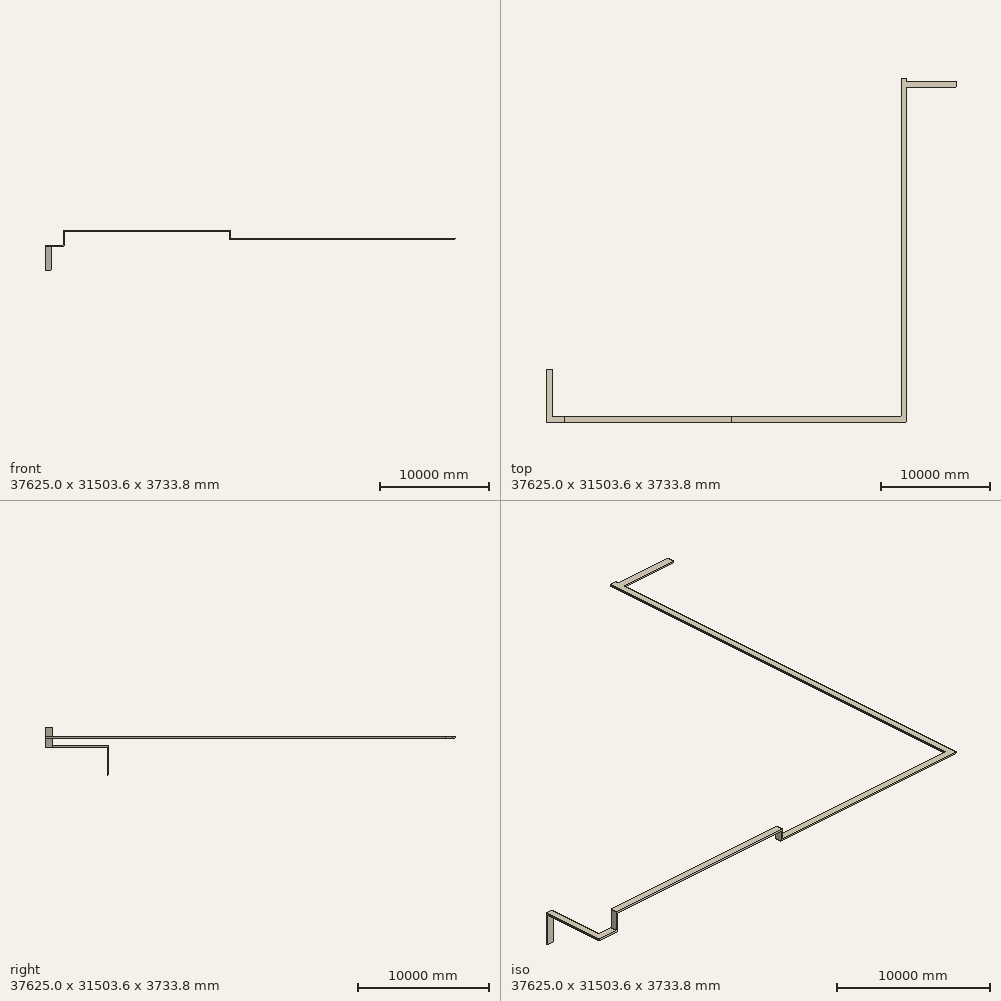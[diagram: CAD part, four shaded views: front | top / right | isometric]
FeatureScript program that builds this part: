
annotation { "Feature Type Name" : "Feature", "Feature Type Description" : "" }
export const myFeature = defineFeature(function(context is Context, id is Id, definition is map)
    precondition{}
    {
        {
            var Q0;
            Q0=qCreatedBy(makeId("Top.planeOp"),FACE);
            var sketch = newSketch(context, id + "F0", { "sketchPlane" : qUnion([Q0])});
            skLineSegment(sketch, "E0.bottom", {"start": v(0, 0) * mm, "end": v(-515.62, 0) * mm});
            skLineSegment(sketch, "E0.top", {"start": v(0, 127) * mm, "end": v(-515.62, 127) * mm});
            skLineSegment(sketch, "E0.left", {"start": v(0, 0) * mm, "end": v(0, 127) * mm});
            skLineSegment(sketch, "E0.right", {"start": v(-515.62, 0) * mm, "end": v(-515.62, 127) * mm});
            skSolve(sketch);
        }
        {
            var Q0;
            Q0=makeQuery(id+"F0.imprint","IMPRINT",FACE,{"disambiguationData":[TD([[makeQuery(id+"F0.imprint","IMPRINT",EDGE,{"derivedFrom":sQuery(id+"F0.wireOp",EDGE,"E0.bottom")}),-1.0]])]});
            extrude(context, id + "F1", {"entities" : qUnion([Q0]), "depth" : 2336.8 * mm});
        }
        {
            var Q0;
            Q0=makeQuery(id+"F1.opExtrude","SWEPT_FACE",FACE,{"disambiguationData":[OSD([sQuery(id+"F0.wireOp",EDGE,"E0.bottom")])]});
            var sketch = newSketch(context, id + "F2", { "sketchPlane" : qUnion([Q0])});
            skLineSegment(sketch, "E1.bottom", {"start": v(-515.62, 2336.8) * mm, "end": v(0, 2336.8) * mm});
            skLineSegment(sketch, "E1.top", {"start": v(-515.62, 2209.8) * mm, "end": v(0, 2209.8) * mm});
            skLineSegment(sketch, "E1.left", {"start": v(-515.62, 2336.8) * mm, "end": v(-515.62, 2209.8) * mm});
            skLineSegment(sketch, "E1.right", {"start": v(0, 2336.8) * mm, "end": v(0, 2209.8) * mm});
            skSolve(sketch);
        }
        {
            var Q0;
            Q0=makeQuery(id+"F2.imprint","IMPRINT",FACE,{"disambiguationData":[TD([[makeQuery(id+"F2.imprint","IMPRINT",EDGE,{"derivedFrom":sQuery(id+"F2.wireOp",EDGE,"E1.bottom")}),1.0]])]});
            extrude(context, id + "F3", {"entities" : qUnion([Q0]), "operationType" : NewBodyOperationType.ADD, "depth" : 4749.8 * mm});
        }
        {
            var Q0;
            Q0=makeQuery(id+"F3.boolean.opBoolean","MERGE",FACE,{"derivedFrom":[makeQuery(id+"F1.opExtrude","SWEPT_FACE",FACE,{"disambiguationData":[OSD([sQuery(id+"F0.wireOp",EDGE,"E0.left")])]}),makeQuery(id+"F3.opExtrude","SWEPT_FACE",FACE,{"disambiguationData":[OSD([sQuery(id+"F2.wireOp",EDGE,"E1.right")])]})]});
            var sketch = newSketch(context, id + "F4", { "sketchPlane" : qUnion([Q0])});
            skLineSegment(sketch, "E2.bottom", {"start": v(-4749.8, 2336.8) * mm, "end": v(-4234.18, 2336.8) * mm});
            skLineSegment(sketch, "E2.top", {"start": v(-4749.8, 2209.8) * mm, "end": v(-4234.18, 2209.8) * mm});
            skLineSegment(sketch, "E2.left", {"start": v(-4749.8, 2336.8) * mm, "end": v(-4749.8, 2209.8) * mm});
            skLineSegment(sketch, "E2.right", {"start": v(-4234.18, 2336.8) * mm, "end": v(-4234.18, 2209.8) * mm});
            skSolve(sketch);
        }
        {
            var Q0;
            Q0=makeQuery(id+"F4.imprint","IMPRINT",FACE,{"disambiguationData":[TD([[makeQuery(id+"F4.imprint","IMPRINT",EDGE,{"derivedFrom":sQuery(id+"F4.wireOp",EDGE,"E2.bottom")}),-1.0]])]});
            extrude(context, id + "F5", {"entities" : qUnion([Q0]), "operationType" : NewBodyOperationType.ADD, "depth" : 1219.2 * mm});
        }
        {
            var Q0;
            Q0=makeQuery(id+"F5.boolean.opBoolean","MERGE",FACE,{"derivedFrom":[makeQuery(id+"F3.boolean.opBoolean","MERGE",FACE,{"derivedFrom":[makeQuery(id+"F1.opExtrude","CAP_FACE",FACE,{"disambiguationData":[OSD([sQuery(id+"F0.wireOp",EDGE,"E0.bottom"),sQuery(id+"F0.wireOp",EDGE,"E0.top"),sQuery(id+"F0.wireOp",EDGE,"E0.left"),sQuery(id+"F0.wireOp",EDGE,"E0.right")])],"isStart":false}),makeQuery(id+"F3.opExtrude","SWEPT_FACE",FACE,{"disambiguationData":[OSD([sQuery(id+"F2.wireOp",EDGE,"E1.bottom")])]})]}),makeQuery(id+"F5.opExtrude","SWEPT_FACE",FACE,{"disambiguationData":[OSD([sQuery(id+"F4.wireOp",EDGE,"E2.bottom")])]})]});
            var sketch = newSketch(context, id + "F6", { "sketchPlane" : qUnion([Q0])});
            skLineSegment(sketch, "E3.bottom", {"start": v(1219.2, -4234.18) * mm, "end": v(1092.2, -4234.18) * mm});
            skLineSegment(sketch, "E3.top", {"start": v(1219.2, -4749.8) * mm, "end": v(1092.2, -4749.8) * mm});
            skLineSegment(sketch, "E3.left", {"start": v(1219.2, -4234.18) * mm, "end": v(1219.2, -4749.8) * mm});
            skLineSegment(sketch, "E3.right", {"start": v(1092.2, -4234.18) * mm, "end": v(1092.2, -4749.8) * mm});
            skSolve(sketch);
        }
        {
            var Q0;
            Q0=makeQuery(id+"F6.imprint","IMPRINT",FACE,{"disambiguationData":[TD([[makeQuery(id+"F6.imprint","IMPRINT",EDGE,{"derivedFrom":sQuery(id+"F6.wireOp",EDGE,"E3.bottom")}),1.0]])]});
            extrude(context, id + "F7", {"entities" : qUnion([Q0]), "operationType" : NewBodyOperationType.ADD, "depth" : 1397 * mm});
        }
        {
            var Q0;
            Q0=makeQuery(id+"F7.boolean.opBoolean","MERGE",FACE,{"derivedFrom":[makeQuery(id+"F5.opExtrude","CAP_FACE",FACE,{"disambiguationData":[OSD([sQuery(id+"F4.wireOp",EDGE,"E2.bottom"),sQuery(id+"F4.wireOp",EDGE,"E2.top"),sQuery(id+"F4.wireOp",EDGE,"E2.left"),sQuery(id+"F4.wireOp",EDGE,"E2.right")])],"isStart":false}),makeQuery(id+"F7.opExtrude","SWEPT_FACE",FACE,{"disambiguationData":[OSD([sQuery(id+"F6.wireOp",EDGE,"E3.left")])]})]});
            var sketch = newSketch(context, id + "F8", { "sketchPlane" : qUnion([Q0])});
            skLineSegment(sketch, "E4.bottom", {"start": v(-4749.8, 3733.8) * mm, "end": v(-4234.18, 3733.8) * mm});
            skLineSegment(sketch, "E4.top", {"start": v(-4749.8, 3606.8) * mm, "end": v(-4234.18, 3606.8) * mm});
            skLineSegment(sketch, "E4.left", {"start": v(-4749.8, 3733.8) * mm, "end": v(-4749.8, 3606.8) * mm});
            skLineSegment(sketch, "E4.right", {"start": v(-4234.18, 3733.8) * mm, "end": v(-4234.18, 3606.8) * mm});
            skSolve(sketch);
        }
        {
            var Q0;
            Q0=makeQuery(id+"F8.imprint","IMPRINT",FACE,{"disambiguationData":[TD([[makeQuery(id+"F8.imprint","IMPRINT",EDGE,{"derivedFrom":sQuery(id+"F8.wireOp",EDGE,"E4.bottom")}),-1.0]])]});
            extrude(context, id + "F9", {"entities" : qUnion([Q0]), "operationType" : NewBodyOperationType.ADD, "depth" : 15240 * mm});
        }
        {
            var Q0;
            Q0=makeQuery(id+"F9.opExtrude","SWEPT_FACE",FACE,{"disambiguationData":[OSD([sQuery(id+"F8.wireOp",EDGE,"E4.top")])]});
            var sketch = newSketch(context, id + "F10", { "sketchPlane" : qUnion([Q0])});
            skLineSegment(sketch, "E5.bottom", {"start": v(16459.2, 4749.8) * mm, "end": v(16332.2, 4749.8) * mm});
            skLineSegment(sketch, "E5.top", {"start": v(16459.2, 4234.18) * mm, "end": v(16332.2, 4234.18) * mm});
            skLineSegment(sketch, "E5.left", {"start": v(16459.2, 4749.8) * mm, "end": v(16459.2, 4234.18) * mm});
            skLineSegment(sketch, "E5.right", {"start": v(16332.2, 4749.8) * mm, "end": v(16332.2, 4234.18) * mm});
            skSolve(sketch);
        }
        {
            var Q0;
            Q0=makeQuery(id+"F10.imprint","IMPRINT",FACE,{"disambiguationData":[TD([[makeQuery(id+"F10.imprint","IMPRINT",EDGE,{"derivedFrom":sQuery(id+"F10.wireOp",EDGE,"E5.bottom")}),1.0]])]});
            extrude(context, id + "F11", {"entities" : qUnion([Q0]), "operationType" : NewBodyOperationType.ADD, "depth" : 736.6 * mm});
        }
        {
            var Q0;
            Q0=makeQuery(id+"F11.boolean.opBoolean","MERGE",FACE,{"derivedFrom":[makeQuery(id+"F9.opExtrude","CAP_FACE",FACE,{"disambiguationData":[OSD([sQuery(id+"F8.wireOp",EDGE,"E4.bottom"),sQuery(id+"F8.wireOp",EDGE,"E4.top"),sQuery(id+"F8.wireOp",EDGE,"E4.left"),sQuery(id+"F8.wireOp",EDGE,"E4.right")])],"isStart":false}),makeQuery(id+"F11.opExtrude","SWEPT_FACE",FACE,{"disambiguationData":[OSD([sQuery(id+"F10.wireOp",EDGE,"E5.left")])]})]});
            var sketch = newSketch(context, id + "F12", { "sketchPlane" : qUnion([Q0])});
            skLineSegment(sketch, "E6.bottom", {"start": v(-4234.18, 2870.2) * mm, "end": v(-4749.8, 2870.2) * mm});
            skLineSegment(sketch, "E6.top", {"start": v(-4234.18, 2997.2) * mm, "end": v(-4749.8, 2997.2) * mm});
            skLineSegment(sketch, "E6.left", {"start": v(-4234.18, 2870.2) * mm, "end": v(-4234.18, 2997.2) * mm});
            skLineSegment(sketch, "E6.right", {"start": v(-4749.8, 2870.2) * mm, "end": v(-4749.8, 2997.2) * mm});
            skSolve(sketch);
        }
        {
            var Q0;
            Q0=makeQuery(id+"F12.imprint","IMPRINT",FACE,{"disambiguationData":[TD([[makeQuery(id+"F12.imprint","IMPRINT",EDGE,{"derivedFrom":sQuery(id+"F12.wireOp",EDGE,"E6.bottom")}),1.0]])]});
            extrude(context, id + "F13", {"entities" : qUnion([Q0]), "operationType" : NewBodyOperationType.ADD, "depth" : 16078.2 * mm});
        }
        {
            var Q0;
            Q0=makeQuery(id+"F13.boolean.opBoolean","MERGE",FACE,{"derivedFrom":[makeQuery(id+"F11.boolean.opBoolean","MERGE",FACE,{"derivedFrom":[makeQuery(id+"F9.boolean.opBoolean","MERGE",FACE,{"derivedFrom":[makeQuery(id+"F7.boolean.opBoolean","MERGE",FACE,{"derivedFrom":[makeQuery(id+"F5.opExtrude","SWEPT_FACE",FACE,{"disambiguationData":[OSD([sQuery(id+"F4.wireOp",EDGE,"E2.right")])]}),makeQuery(id+"F7.opExtrude","SWEPT_FACE",FACE,{"disambiguationData":[OSD([sQuery(id+"F6.wireOp",EDGE,"E3.bottom")])]})]}),makeQuery(id+"F9.opExtrude","SWEPT_FACE",FACE,{"disambiguationData":[OSD([sQuery(id+"F8.wireOp",EDGE,"E4.right")])]})]}),makeQuery(id+"F11.opExtrude","SWEPT_FACE",FACE,{"disambiguationData":[OSD([sQuery(id+"F10.wireOp",EDGE,"E5.top")])]})]}),makeQuery(id+"F13.opExtrude","SWEPT_FACE",FACE,{"disambiguationData":[OSD([sQuery(id+"F12.wireOp",EDGE,"E6.left")])]})]});
            var sketch = newSketch(context, id + "F14", { "sketchPlane" : qUnion([Q0])});
            skLineSegment(sketch, "E7.bottom", {"start": v(-32537.4, 2997.2) * mm, "end": v(-32021.78, 2997.2) * mm});
            skLineSegment(sketch, "E7.top", {"start": v(-32537.4, 2870.2) * mm, "end": v(-32021.78, 2870.2) * mm});
            skLineSegment(sketch, "E7.left", {"start": v(-32537.4, 2997.2) * mm, "end": v(-32537.4, 2870.2) * mm});
            skLineSegment(sketch, "E7.right", {"start": v(-32021.78, 2997.2) * mm, "end": v(-32021.78, 2870.2) * mm});
            skSolve(sketch);
        }
        {
            var Q0;
            Q0=makeQuery(id+"F14.imprint","IMPRINT",FACE,{"disambiguationData":[TD([[makeQuery(id+"F14.imprint","IMPRINT",EDGE,{"derivedFrom":sQuery(id+"F14.wireOp",EDGE,"E7.bottom")}),-1.0]])]});
            extrude(context, id + "F15", {"entities" : qUnion([Q0]), "operationType" : NewBodyOperationType.ADD, "depth" : 30734 * mm});
        }
        {
            var Q0;
            Q0=makeQuery(id+"F15.boolean.opBoolean","MERGE",FACE,{"derivedFrom":[makeQuery(id+"F13.opExtrude","CAP_FACE",FACE,{"disambiguationData":[OSD([sQuery(id+"F12.wireOp",EDGE,"E6.bottom"),sQuery(id+"F12.wireOp",EDGE,"E6.top"),sQuery(id+"F12.wireOp",EDGE,"E6.left"),sQuery(id+"F12.wireOp",EDGE,"E6.right")])],"isStart":false}),makeQuery(id+"F15.opExtrude","SWEPT_FACE",FACE,{"disambiguationData":[OSD([sQuery(id+"F14.wireOp",EDGE,"E7.left")])]})]});
            var sketch = newSketch(context, id + "F16", { "sketchPlane" : qUnion([Q0])});
            skLineSegment(sketch, "E8.bottom", {"start": v(26499.82, 2870.2) * mm, "end": v(25984.2, 2870.2) * mm});
            skLineSegment(sketch, "E8.top", {"start": v(26499.82, 2997.2) * mm, "end": v(25984.2, 2997.2) * mm});
            skLineSegment(sketch, "E8.left", {"start": v(26499.82, 2870.2) * mm, "end": v(26499.82, 2997.2) * mm});
            skLineSegment(sketch, "E8.right", {"start": v(25984.2, 2870.2) * mm, "end": v(25984.2, 2997.2) * mm});
            skSolve(sketch);
        }
        {
            var Q0;
            Q0=makeQuery(id+"F16.imprint","IMPRINT",FACE,{"disambiguationData":[TD([[makeQuery(id+"F16.imprint","IMPRINT",EDGE,{"derivedFrom":sQuery(id+"F16.wireOp",EDGE,"E8.bottom")}),1.0]])]});
            extrude(context, id + "F17", {"entities" : qUnion([Q0]), "operationType" : NewBodyOperationType.ADD, "depth" : 3048 * mm});
        }
        {
            var Q0;
            Q0=makeQuery(id+"F17.boolean.opBoolean","MERGE",FACE,{"derivedFrom":[makeQuery(id+"F15.opExtrude","CAP_FACE",FACE,{"disambiguationData":[OSD([sQuery(id+"F14.wireOp",EDGE,"E7.bottom"),sQuery(id+"F14.wireOp",EDGE,"E7.top"),sQuery(id+"F14.wireOp",EDGE,"E7.left"),sQuery(id+"F14.wireOp",EDGE,"E7.right")])],"isStart":false}),makeQuery(id+"F17.opExtrude","SWEPT_FACE",FACE,{"disambiguationData":[OSD([sQuery(id+"F16.wireOp",EDGE,"E8.left")])]})]});
            var sketch = newSketch(context, id + "F18", { "sketchPlane" : qUnion([Q0])});
            skLineSegment(sketch, "E9.bottom", {"start": v(-32021.78, 2870.2) * mm, "end": v(-32537.4, 2870.2) * mm});
            skLineSegment(sketch, "E9.top", {"start": v(-32021.78, 2997.2) * mm, "end": v(-32537.4, 2997.2) * mm});
            skLineSegment(sketch, "E9.left", {"start": v(-32021.78, 2870.2) * mm, "end": v(-32021.78, 2997.2) * mm});
            skLineSegment(sketch, "E9.right", {"start": v(-32537.4, 2870.2) * mm, "end": v(-32537.4, 2997.2) * mm});
            skSolve(sketch);
        }
        {
            var Q0;
            Q0=makeQuery(id+"F18.imprint","IMPRINT",FACE,{"disambiguationData":[TD([[makeQuery(id+"F18.imprint","IMPRINT",EDGE,{"derivedFrom":sQuery(id+"F18.wireOp",EDGE,"E9.bottom")}),1.0]])]});
            extrude(context, id + "F19", {"entities" : qUnion([Q0]), "operationType" : NewBodyOperationType.ADD, "depth" : 254 * mm});
        }
        {
            var Q0;
            Q0=makeQuery(id+"F17.opExtrude","CAP_FACE",FACE,{"disambiguationData":[OSD([sQuery(id+"F16.wireOp",EDGE,"E8.bottom"),sQuery(id+"F16.wireOp",EDGE,"E8.top"),sQuery(id+"F16.wireOp",EDGE,"E8.left"),sQuery(id+"F16.wireOp",EDGE,"E8.right")])],"isStart":false});
            extrude(context, id + "F20", {"entities" : qUnion([Q0]), "operationType" : NewBodyOperationType.ADD, "depth" : 1524 * mm});
        }
    });
